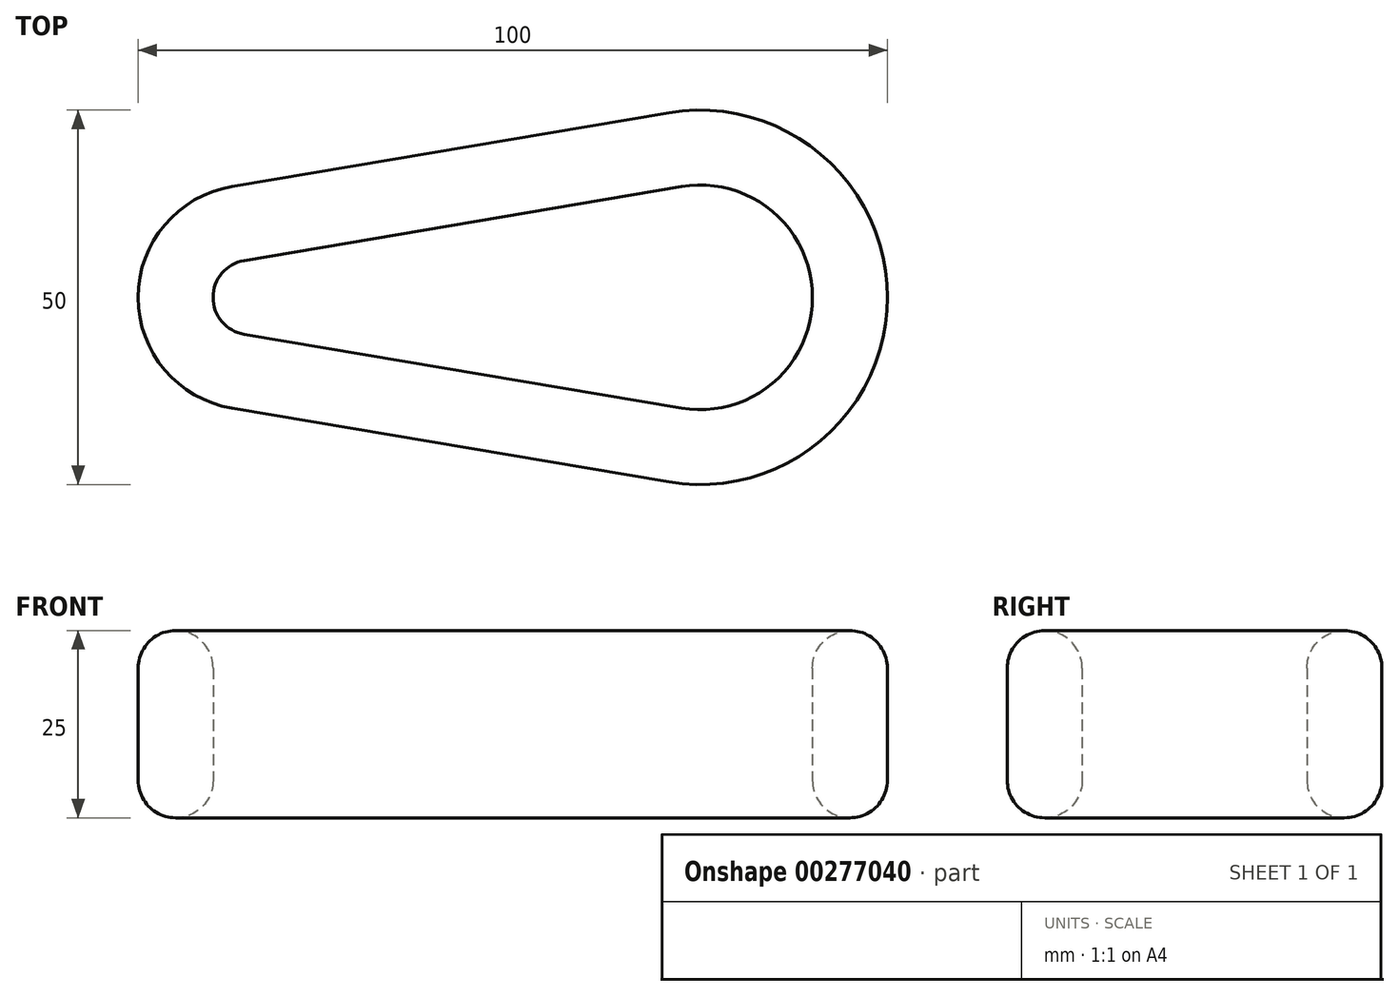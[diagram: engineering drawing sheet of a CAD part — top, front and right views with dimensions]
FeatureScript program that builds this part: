
annotation { "Feature Type Name" : "Feature", "Feature Type Description" : "" }
export const myFeature = defineFeature(function(context is Context, id is Id, definition is map)
    precondition{}
    {
        {
            var Q0;
            Q0=qCreatedBy(makeId("Top.planeOp"),FACE);
            var sketch = newSketch(context, id + "F0", { "sketchPlane" : qUnion([Q0])});
            skArc(sketch, "E0", {"start": v(-62.5, 14.8) * mm, "mid": v(-75, 0) * mm, "end": v(-62.5, -14.8) * mm});
            skArc(sketch, "E1", {"start": v(-4.17, -24.65) * mm, "mid": v(25, 0) * mm, "end": v(-4.17, 24.65) * mm});
            skLineSegment(sketch, "E2", {"start": v(-4.17, 24.65) * mm, "end": v(-62.5, 14.8) * mm});
            skLineSegment(sketch, "E3", {"start": v(-141, 0) * mm, "end": v(79.99, 0) * mm, "construction": true});
            skLineSegment(sketch, "E4.MirrorCS", {"start": v(-4.17, -24.65) * mm, "end": v(-62.5, -14.8) * mm});
            skLineSegment(sketch, "E5.0", {"start": v(-2.5, 14.8) * mm, "end": v(-60.83, 4.93) * mm});
            skArc(sketch, "E5.1", {"start": v(-2.5, -14.8) * mm, "mid": v(15, 0) * mm, "end": v(-2.5, 14.8) * mm});
            skLineSegment(sketch, "E5.2", {"start": v(-2.5, -14.8) * mm, "end": v(-60.83, -4.93) * mm});
            skArc(sketch, "E5.3", {"start": v(-60.83, 4.93) * mm, "mid": v(-65, 0) * mm, "end": v(-60.83, -4.93) * mm});
            skSolve(sketch);
        }
        {
            var Q0;
            Q0 = qSketchRegion(id + "F0", true);
            extrude(context, id + "F1", {"entities" : qUnion([Q0]), "depth" : 25 * mm});
        }
        {
            var Q0;
            Q0=makeQuery(id+"F1.opExtrude","CAP_EDGE",EDGE,{"disambiguationData":[OSD([sQuery(id+"F0.wireOp",EDGE,"E4.MirrorCS")])],"isStart":false});
            var Q1;
            Q1=makeQuery(id+"F1.opExtrude","CAP_EDGE",EDGE,{"disambiguationData":[OSD([sQuery(id+"F0.wireOp",EDGE,"E1")])],"isStart":false});
            var Q2;
            Q2=makeQuery(id+"F1.opExtrude","CAP_EDGE",EDGE,{"disambiguationData":[OSD([sQuery(id+"F0.wireOp",EDGE,"E4.MirrorCS")])],"isStart":true});
            var Q3;
            Q3=makeQuery(id+"F1.opExtrude","CAP_EDGE",EDGE,{"disambiguationData":[OSD([sQuery(id+"F0.wireOp",EDGE,"E1")])],"isStart":true});
            fillet(context, id + "F2", {"entities" : qUnion([Q0, Q1, Q2, Q3]), "radius" : 5 * mm, "tangentPropagation" : true, "allowEdgeOverflow" : false});
        }
        {
            var Q0;
            Q0=makeQuery(id+"F1.opExtrude","CAP_EDGE",EDGE,{"disambiguationData":[OSD([sQuery(id+"F0.wireOp",EDGE,"E5.0")])],"isStart":false});
            fillet(context, id + "F3", {"entities" : qUnion([Q0]), "radius" : 5 * mm, "tangentPropagation" : true, "allowEdgeOverflow" : false});
        }
        {
            var Q0;
            Q0=makeQuery(id+"F1.opExtrude","CAP_EDGE",EDGE,{"disambiguationData":[OSD([sQuery(id+"F0.wireOp",EDGE,"E5.1")])],"isStart":true});
            var Q1;
            Q1=makeQuery(id+"F1.opExtrude","CAP_EDGE",EDGE,{"disambiguationData":[OSD([sQuery(id+"F0.wireOp",EDGE,"E5.0")])],"isStart":true});
            fillet(context, id + "F4", {"entities" : qUnion([Q0, Q1]), "radius" : 5 * mm, "tangentPropagation" : true, "allowEdgeOverflow" : false});
        }
    });
